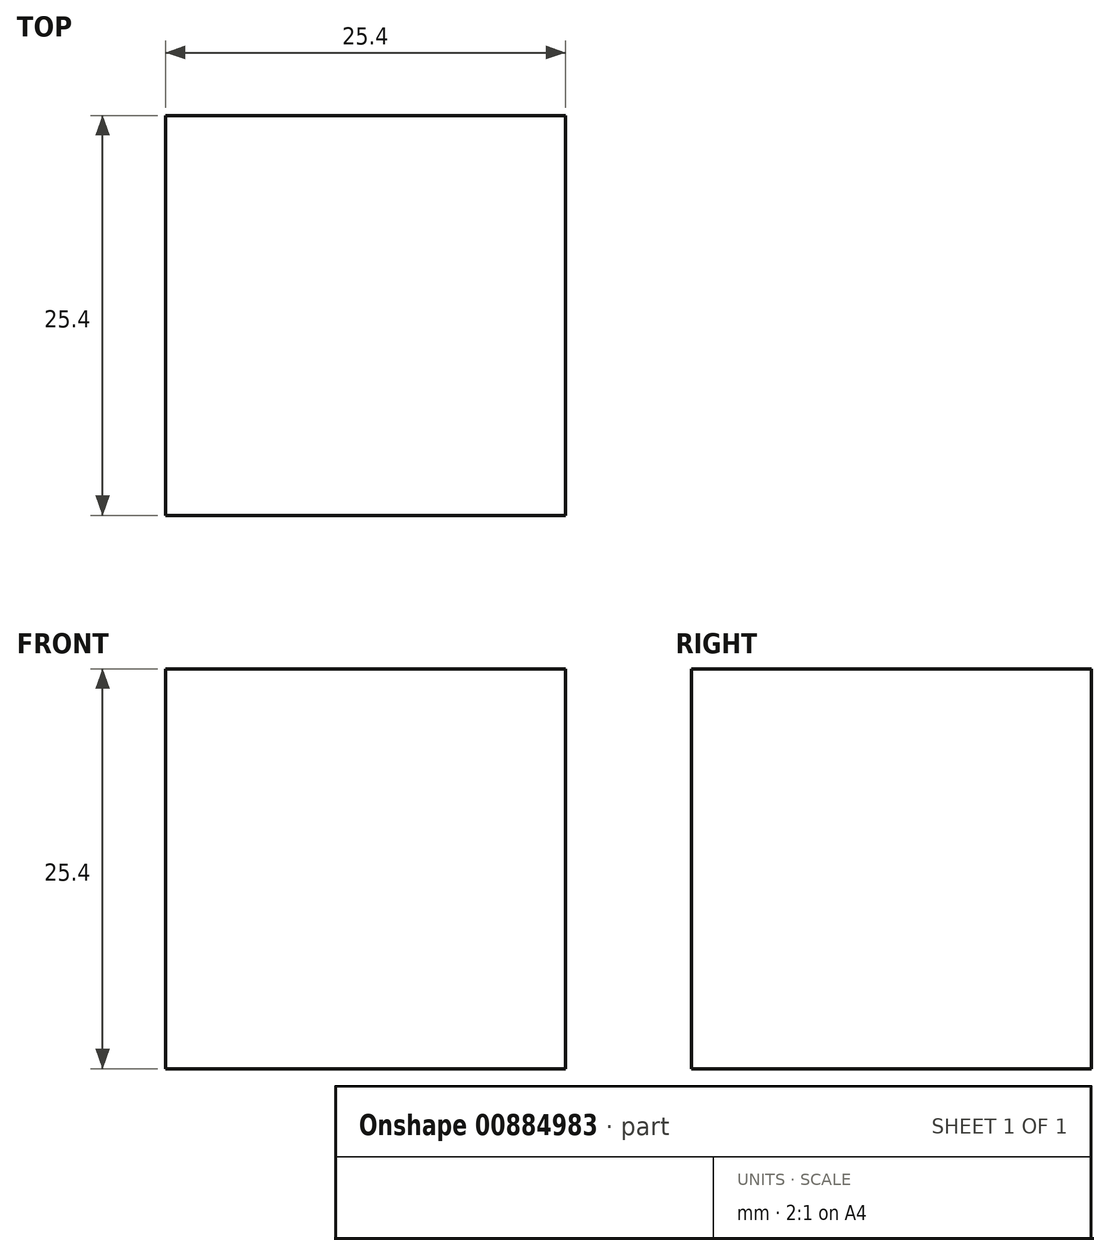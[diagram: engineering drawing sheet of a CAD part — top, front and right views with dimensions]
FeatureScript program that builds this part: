
annotation { "Feature Type Name" : "Feature", "Feature Type Description" : "" }
export const myFeature = defineFeature(function(context is Context, id is Id, definition is map)
    precondition{}
    {
        {
            var Q0;
            Q0=qCreatedBy(makeId("Front.planeOp"),FACE);
            var sketch = newSketch(context, id + "F0", { "sketchPlane" : qUnion([Q0])});
            skLineSegment(sketch, "E0.bottom", {"start": v(0, 0) * mm, "end": v(25.4, 0) * mm});
            skLineSegment(sketch, "E0.top", {"start": v(0, 25.4) * mm, "end": v(25.4, 25.4) * mm});
            skLineSegment(sketch, "E0.left", {"start": v(0, 0) * mm, "end": v(0, 25.4) * mm});
            skLineSegment(sketch, "E0.right", {"start": v(25.4, 0) * mm, "end": v(25.4, 25.4) * mm});
            skSolve(sketch);
        }
        {
            var Q0;
            Q0=makeQuery(id+"F0.imprint","IMPRINT",FACE,{"disambiguationData":[TD([[makeQuery(id+"F0.imprint","IMPRINT",EDGE,{"derivedFrom":sQuery(id+"F0.wireOp",EDGE,"E0.bottom")}),1.0]])]});
            extrude(context, id + "F1", {"entities" : qUnion([Q0]), "oppositeDirection" : true, "depth" : 25.4 * mm, "offsetDistance" : 25.4 * mm});
        }
    });
